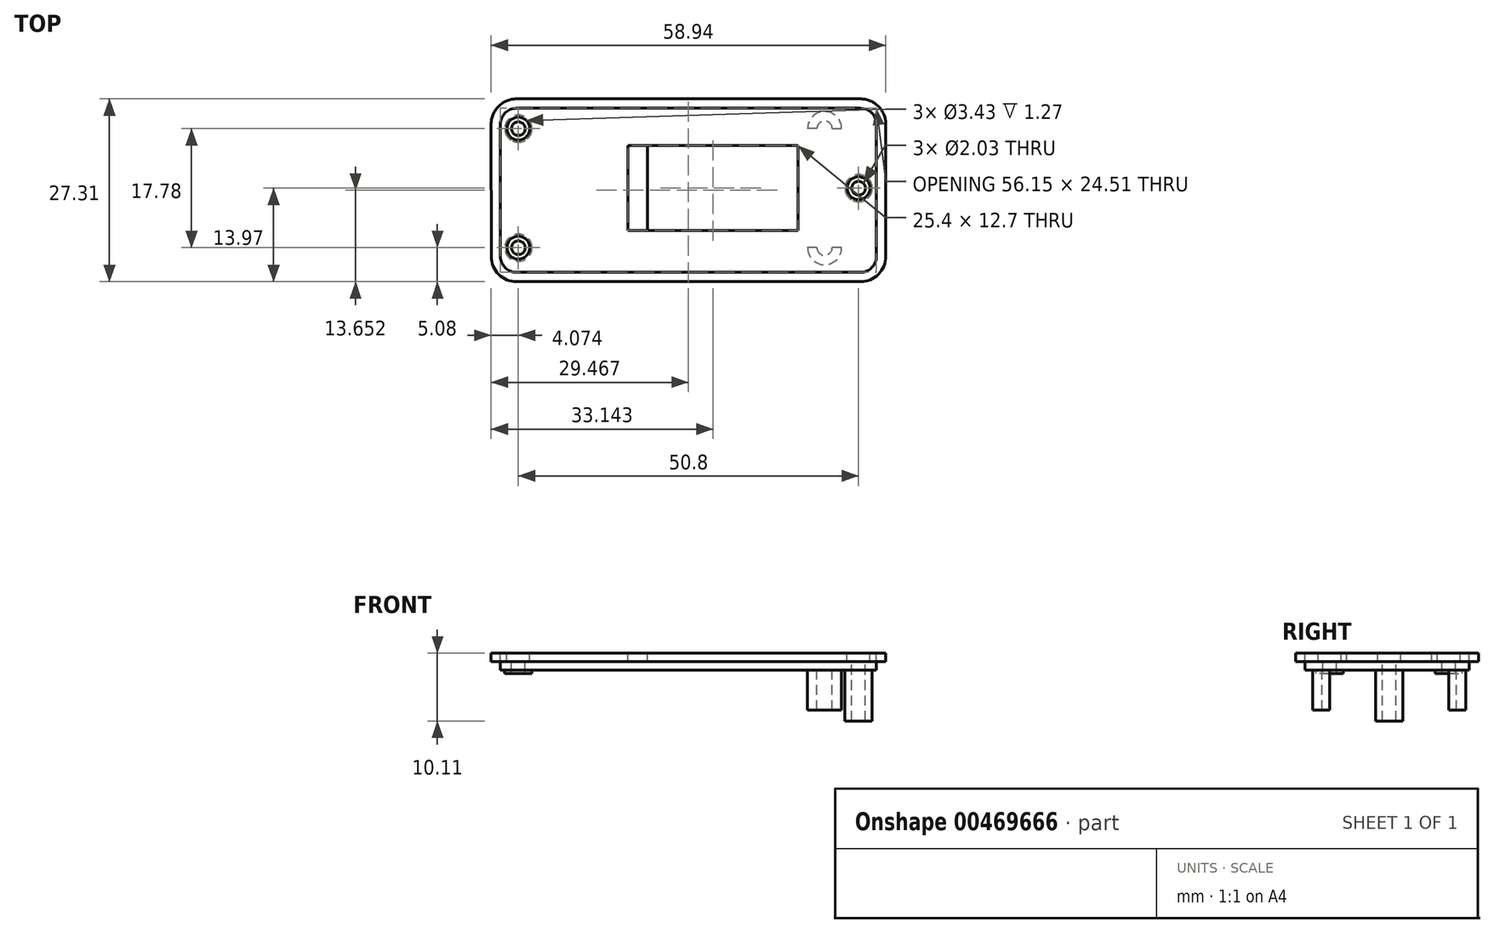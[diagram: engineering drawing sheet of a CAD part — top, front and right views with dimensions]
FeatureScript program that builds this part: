
annotation { "Feature Type Name" : "Feature", "Feature Type Description" : "" }
export const myFeature = defineFeature(function(context is Context, id is Id, definition is map)
    precondition{}
    {
        {
            var Q0;
            Q0=qCreatedBy(makeId("Top.planeOp"),FACE);
            var sketch = newSketch(context, id + "F0", { "sketchPlane" : qUnion([Q0])});
            skLineSegment(sketch, "E0.bottom", {"start": v(29.72, -13.97) * mm, "end": v(-21.58, -13.97) * mm});
            skLineSegment(sketch, "E0.top", {"start": v(29.72, 13.34) * mm, "end": v(-21.6, 13.34) * mm});
            skLineSegment(sketch, "E0.left", {"start": v(33.53, -10.16) * mm, "end": v(33.53, 9.52) * mm});
            skPoint(sketch, "E0.middle", {"position": v(1.52, 0) * mm});
            skLineSegment(sketch, "E1", {"start": v(-25.41, 9.52) * mm, "end": v(-25.39, -10.16) * mm});
            skLineSegment(sketch, "E2.bottom", {"start": v(-21.6, 11.94) * mm, "end": v(29.72, 11.94) * mm});
            skLineSegment(sketch, "E2.top", {"start": v(-21.6, -12.57) * mm, "end": v(29.72, -12.57) * mm});
            skLineSegment(sketch, "E2.left", {"start": v(-24.02, 9.53) * mm, "end": v(-24.02, -10.16) * mm});
            skLineSegment(sketch, "E2.right", {"start": v(32.13, 9.53) * mm, "end": v(32.13, -10.16) * mm});
            skPoint(sketch, "E3.visualSharp", {"position": v(-24.02, 11.94) * mm});
            skArc(sketch, "E3.filletArc", {"start": v(-21.6, 11.94) * mm, "mid": v(-23.31, 11.23) * mm, "end": v(-24.02, 9.53) * mm});
            skPoint(sketch, "E4.visualSharp", {"position": v(-24.02, -12.57) * mm});
            skArc(sketch, "E4.filletArc", {"start": v(-24.02, -10.16) * mm, "mid": v(-23.31, -11.87) * mm, "end": v(-21.6, -12.57) * mm});
            skPoint(sketch, "E5.visualSharp", {"position": v(32.13, -12.57) * mm});
            skArc(sketch, "E5.filletArc", {"start": v(29.72, -12.57) * mm, "mid": v(31.42, -11.87) * mm, "end": v(32.13, -10.16) * mm});
            skPoint(sketch, "E6.visualSharp", {"position": v(32.13, 11.94) * mm});
            skArc(sketch, "E6.filletArc", {"start": v(32.13, 9.53) * mm, "mid": v(31.42, 11.23) * mm, "end": v(29.72, 11.94) * mm});
            skPoint(sketch, "E7.visualSharp", {"position": v(-25.41, 13.34) * mm});
            skArc(sketch, "E7.filletArc", {"start": v(-21.6, 13.34) * mm, "mid": v(-24.3, 12.22) * mm, "end": v(-25.41, 9.52) * mm});
            skPoint(sketch, "E8.visualSharp", {"position": v(-25.39, -13.97) * mm});
            skArc(sketch, "E8.filletArc", {"start": v(-25.39, -10.16) * mm, "mid": v(-24.27, -12.86) * mm, "end": v(-21.58, -13.97) * mm});
            skPoint(sketch, "E9.visualSharp", {"position": v(33.53, -13.97) * mm});
            skArc(sketch, "E9.filletArc", {"start": v(29.72, -13.97) * mm, "mid": v(32.41, -12.85) * mm, "end": v(33.53, -10.16) * mm});
            skPoint(sketch, "E10.visualSharp", {"position": v(33.53, 13.34) * mm});
            skArc(sketch, "E10.filletArc", {"start": v(33.53, 9.52) * mm, "mid": v(32.41, 12.22) * mm, "end": v(29.72, 13.34) * mm});
            skLineSegment(sketch, "E11.bottom", {"start": v(20.43, -6.35) * mm, "end": v(-4.97, -6.35) * mm});
            skLineSegment(sketch, "E11.top", {"start": v(20.43, 6.35) * mm, "end": v(-4.97, 6.35) * mm});
            skLineSegment(sketch, "E11.left", {"start": v(20.43, -6.35) * mm, "end": v(20.43, 6.35) * mm});
            skLineSegment(sketch, "E11.right", {"start": v(-4.97, -6.35) * mm, "end": v(-4.97, 6.35) * mm});
            skPoint(sketch, "E11.middle", {"position": v(7.73, 0) * mm});
            skLineSegment(sketch, "E12.bottom", {"start": v(-4.97, 6.35) * mm, "end": v(-2.05, 6.35) * mm});
            skLineSegment(sketch, "E12.top", {"start": v(-4.97, -6.35) * mm, "end": v(-2.05, -6.35) * mm});
            skLineSegment(sketch, "E12.left", {"start": v(-4.97, 6.35) * mm, "end": v(-4.97, -6.35) * mm});
            skLineSegment(sketch, "E12.right", {"start": v(-2.05, 6.35) * mm, "end": v(-2.05, -6.35) * mm});
            skCircle(sketch, "E13", {"center": v(10.8, 0) * mm, "radius": 4.76 * mm});
            skSolve(sketch);
        }
        {
            var Q0;
            Q0=makeQuery(id+"F0.imprint","IMPRINT",FACE,{"disambiguationData":[TD([[makeQuery(id+"F0.imprint","IMPRINT",EDGE,{"derivedFrom":sQuery(id+"F0.wireOp",EDGE,"E2.bottom")}),-1.0]])]});
            extrude(context, id + "F1", {"entities" : qUnion([Q0]), "depth" : -2.54 * mm});
        }
        {
            var Q0;
            Q0=makeQuery(id+"F0.imprint","IMPRINT",FACE,{"disambiguationData":[TD([[makeQuery(id+"F0.imprint","IMPRINT",EDGE,{"derivedFrom":sQuery(id+"F0.wireOp",EDGE,"E11.bottom")}),-1.0]])]});
            extrude(context, id + "F2", {"entities" : qUnion([Q0]), "depth" : -1.27 * mm});
        }
        {
            var Q0;
            Q0=makeQuery(id+"F0.imprint","IMPRINT",FACE,{"disambiguationData":[TD([[makeQuery(id+"F0.imprint","IMPRINT",EDGE,{"derivedFrom":sQuery(id+"F0.wireOp",EDGE,"E0.bottom")}),-1.0]])]});
            extrude(context, id + "F3", {"entities" : qUnion([Q0]), "depth" : -1.27 * mm});
        }
        {
            var Q0;
            Q0=makeQuery(id+"F1.opExtrude","CAP_FACE",FACE,{"disambiguationData":[OSD([sQuery(id+"F0.wireOp",EDGE,"E2.bottom"),sQuery(id+"F0.wireOp",EDGE,"E2.top"),sQuery(id+"F0.wireOp",EDGE,"E2.left"),sQuery(id+"F0.wireOp",EDGE,"E2.right"),sQuery(id+"F0.wireOp",EDGE,"E3.filletArc"),sQuery(id+"F0.wireOp",EDGE,"E4.filletArc"),sQuery(id+"F0.wireOp",EDGE,"E5.filletArc"),sQuery(id+"F0.wireOp",EDGE,"E6.filletArc")])],"isStart":false});
            var sketch = newSketch(context, id + "F4", { "sketchPlane" : qUnion([Q0])});
            skCircle(sketch, "E14", {"center": v(-21.34, 8.89) * mm, "radius": 2.03 * mm});
            skCircle(sketch, "E15", {"center": v(24.38, 8.9) * mm, "radius": 1.14 * mm});
            skCircle(sketch, "E16", {"center": v(-21.34, -8.89) * mm, "radius": 2.03 * mm});
            skCircle(sketch, "E17", {"center": v(24.38, -8.89) * mm, "radius": 1.14 * mm});
            skLineSegment(sketch, "E18", {"start": v(24.38, -8.89) * mm, "end": v(26.92, -8.89) * mm});
            skLineSegment(sketch, "E19", {"start": v(26.92, 8.9) * mm, "end": v(24.38, 8.9) * mm});
            skLineSegment(sketch, "E20", {"start": v(24.38, -8.89) * mm, "end": v(21.84, -8.89) * mm});
            skLineSegment(sketch, "E21", {"start": v(24.38, 8.9) * mm, "end": v(21.84, 8.9) * mm});
            skArc(sketch, "E22", {"start": v(21.84, -8.89) * mm, "mid": v(24.38, -11.43) * mm, "end": v(26.92, -8.89) * mm});
            skArc(sketch, "E23", {"start": v(26.92, 8.9) * mm, "mid": v(24.38, 11.43) * mm, "end": v(21.84, 8.9) * mm});
            skSolve(sketch);
        }
        {
            var Q0;
            Q0=makeQuery(id+"F4.imprint","IMPRINT",FACE,{"disambiguationData":[TD([[makeQuery(id+"F4.imprint","IMPRINT",EDGE,{"derivedFrom":sQuery(id+"F4.wireOp",EDGE,"E14")}),1.0]])]});
            var Q1;
            Q1=makeQuery(id+"F4.imprint","IMPRINT",FACE,{"disambiguationData":[TD([[makeQuery(id+"F4.imprint","IMPRINT",EDGE,{"derivedFrom":sQuery(id+"F4.wireOp",EDGE,"E16")}),1.0]])]});
            var Q2;
            Q2=sQuery(id+"F4.wireOp",EDGE,"E16");
            var Q3;
            Q3=sQuery(id+"F4.wireOp",EDGE,"E14");
            extrude(context, id + "F5", {"entities" : qUnion([Q0, Q1]), "operationType" : NewBodyOperationType.ADD, "surfaceEntities" : qUnion([Q2, Q3]), "depth" : 0.46 * mm});
        }
        {
            var Q0;
            {var subQ5=sQuery(id+"F4.wireOp",EDGE,"E23");Q0=makeQuery(id+"F4.imprint","IMPRINT",FACE,{"disambiguationData":[TD([[makeQuery(id+"F4.imprint","IMPRINT",EDGE,{"derivedFrom":subQ5}),1.0]])]});}
            var Q1;
            {var subQ5=sQuery(id+"F4.wireOp",EDGE,"E22");Q1=makeQuery(id+"F4.imprint","IMPRINT",FACE,{"disambiguationData":[TD([[makeQuery(id+"F4.imprint","IMPRINT",EDGE,{"derivedFrom":subQ5}),1.0]])]});}
            extrude(context, id + "F6", {"entities" : qUnion([Q0, Q1]), "operationType" : NewBodyOperationType.ADD, "depth" : 5.97 * mm});
        }
        {
            var Q0;
            Q0=makeQuery(id+"F1.opExtrude","CAP_FACE",FACE,{"disambiguationData":[OSD([sQuery(id+"F0.wireOp",EDGE,"E2.bottom"),sQuery(id+"F0.wireOp",EDGE,"E2.top"),sQuery(id+"F0.wireOp",EDGE,"E2.left"),sQuery(id+"F0.wireOp",EDGE,"E2.right"),sQuery(id+"F0.wireOp",EDGE,"E3.filletArc"),sQuery(id+"F0.wireOp",EDGE,"E4.filletArc"),sQuery(id+"F0.wireOp",EDGE,"E5.filletArc"),sQuery(id+"F0.wireOp",EDGE,"E6.filletArc")])],"isStart":true});
            var sketch = newSketch(context, id + "F7", { "sketchPlane" : qUnion([Q0])});
            skCircle(sketch, "E24", {"center": v(-21.34, 8.89) * mm, "radius": 1.71 * mm});
            skCircle(sketch, "E25", {"center": v(-21.34, -8.9) * mm, "radius": 1.71 * mm});
            skCircle(sketch, "E26", {"center": v(29.46, 0) * mm, "radius": 1.71 * mm});
            skSolve(sketch);
        }
        {
            var Q0;
            Q0=makeQuery(id+"F7.imprint","IMPRINT",FACE,{"disambiguationData":[TD([[makeQuery(id+"F7.imprint","IMPRINT",EDGE,{"derivedFrom":sQuery(id+"F7.wireOp",EDGE,"E24")}),1.0]])]});
            var Q1;
            Q1=makeQuery(id+"F7.imprint","IMPRINT",FACE,{"disambiguationData":[TD([[makeQuery(id+"F7.imprint","IMPRINT",EDGE,{"derivedFrom":sQuery(id+"F7.wireOp",EDGE,"E25")}),1.0]])]});
            var Q2;
            Q2=makeQuery(id+"F7.imprint","IMPRINT",FACE,{"disambiguationData":[TD([[makeQuery(id+"F7.imprint","IMPRINT",EDGE,{"derivedFrom":sQuery(id+"F7.wireOp",EDGE,"E26")}),1.0]])]});
            var Q3;
            Q3=sQuery(id+"F7.wireOp",EDGE,"E24");
            var Q4;
            Q4=sQuery(id+"F7.wireOp",EDGE,"E25");
            extrude(context, id + "F8", {"entities" : qUnion([Q0, Q1, Q2]), "operationType" : NewBodyOperationType.REMOVE, "surfaceEntities" : qUnion([Q3, Q4]), "oppositeDirection" : true, "offsetDistance" : 25.4 * mm, "depth" : 1.27 * mm});
        }
        {
            var Q0;
            Q0=makeQuery(id+"F3.opExtrude","CAP_FACE",FACE,{"disambiguationData":[OSD([sQuery(id+"F0.wireOp",EDGE,"E0.bottom"),sQuery(id+"F0.wireOp",EDGE,"E0.top"),sQuery(id+"F0.wireOp",EDGE,"E0.left"),sQuery(id+"F0.wireOp",EDGE,"E1"),sQuery(id+"F0.wireOp",EDGE,"E2.bottom"),sQuery(id+"F0.wireOp",EDGE,"E2.top"),sQuery(id+"F0.wireOp",EDGE,"E2.left"),sQuery(id+"F0.wireOp",EDGE,"E2.right"),sQuery(id+"F0.wireOp",EDGE,"E3.filletArc"),sQuery(id+"F0.wireOp",EDGE,"E4.filletArc"),sQuery(id+"F0.wireOp",EDGE,"E5.filletArc"),sQuery(id+"F0.wireOp",EDGE,"E6.filletArc"),sQuery(id+"F0.wireOp",EDGE,"E7.filletArc"),sQuery(id+"F0.wireOp",EDGE,"E8.filletArc"),sQuery(id+"F0.wireOp",EDGE,"E9.filletArc"),sQuery(id+"F0.wireOp",EDGE,"E10.filletArc")])],"isStart":false});
            var sketch = newSketch(context, id + "F9", { "sketchPlane" : qUnion([Q0])});
            skCircle(sketch, "E27", {"center": v(-21.34, 8.9) * mm, "radius": 1.02 * mm});
            skCircle(sketch, "E28", {"center": v(-21.34, -8.9) * mm, "radius": 1.02 * mm});
            skCircle(sketch, "E29", {"center": v(29.46, 0) * mm, "radius": 1.02 * mm});
            skSolve(sketch);
        }
        {
            var Q0;
            Q0 = qSketchRegion(id + "F9", true);
            extrude(context, id + "F10", {"entities" : qUnion([Q0]), "operationType" : NewBodyOperationType.REMOVE, "oppositeDirection" : true, "depth" : -5.97 * mm});
        }
        {
            var Q0;
            Q0=makeQuery(id+"F1.opExtrude","CAP_FACE",FACE,{"disambiguationData":[OSD([sQuery(id+"F0.wireOp",EDGE,"E2.bottom"),sQuery(id+"F0.wireOp",EDGE,"E2.top"),sQuery(id+"F0.wireOp",EDGE,"E2.left"),sQuery(id+"F0.wireOp",EDGE,"E2.right"),sQuery(id+"F0.wireOp",EDGE,"E3.filletArc"),sQuery(id+"F0.wireOp",EDGE,"E4.filletArc"),sQuery(id+"F0.wireOp",EDGE,"E5.filletArc"),sQuery(id+"F0.wireOp",EDGE,"E6.filletArc")])],"isStart":false});
            var sketch = newSketch(context, id + "F11", { "sketchPlane" : qUnion([Q0])});
            skCircle(sketch, "E30", {"center": v(29.46, 0) * mm, "radius": 2.03 * mm});
            skSolve(sketch);
        }
        {
            var Q0;
            Q0=makeQuery(id+"F11.imprint","IMPRINT",FACE,{"disambiguationData":[TD([[makeQuery(id+"F11.imprint","IMPRINT",EDGE,{"derivedFrom":sQuery(id+"F11.wireOp",EDGE,"E30")}),1.0]])]});
            var Q1;
            Q1=sQuery(id+"F11.wireOp",EDGE,"E30");
            extrude(context, id + "F12", {"entities" : qUnion([Q0]), "operationType" : NewBodyOperationType.ADD, "surfaceEntities" : qUnion([Q1]), "depth" : 7.57 * mm});
        }
    });
